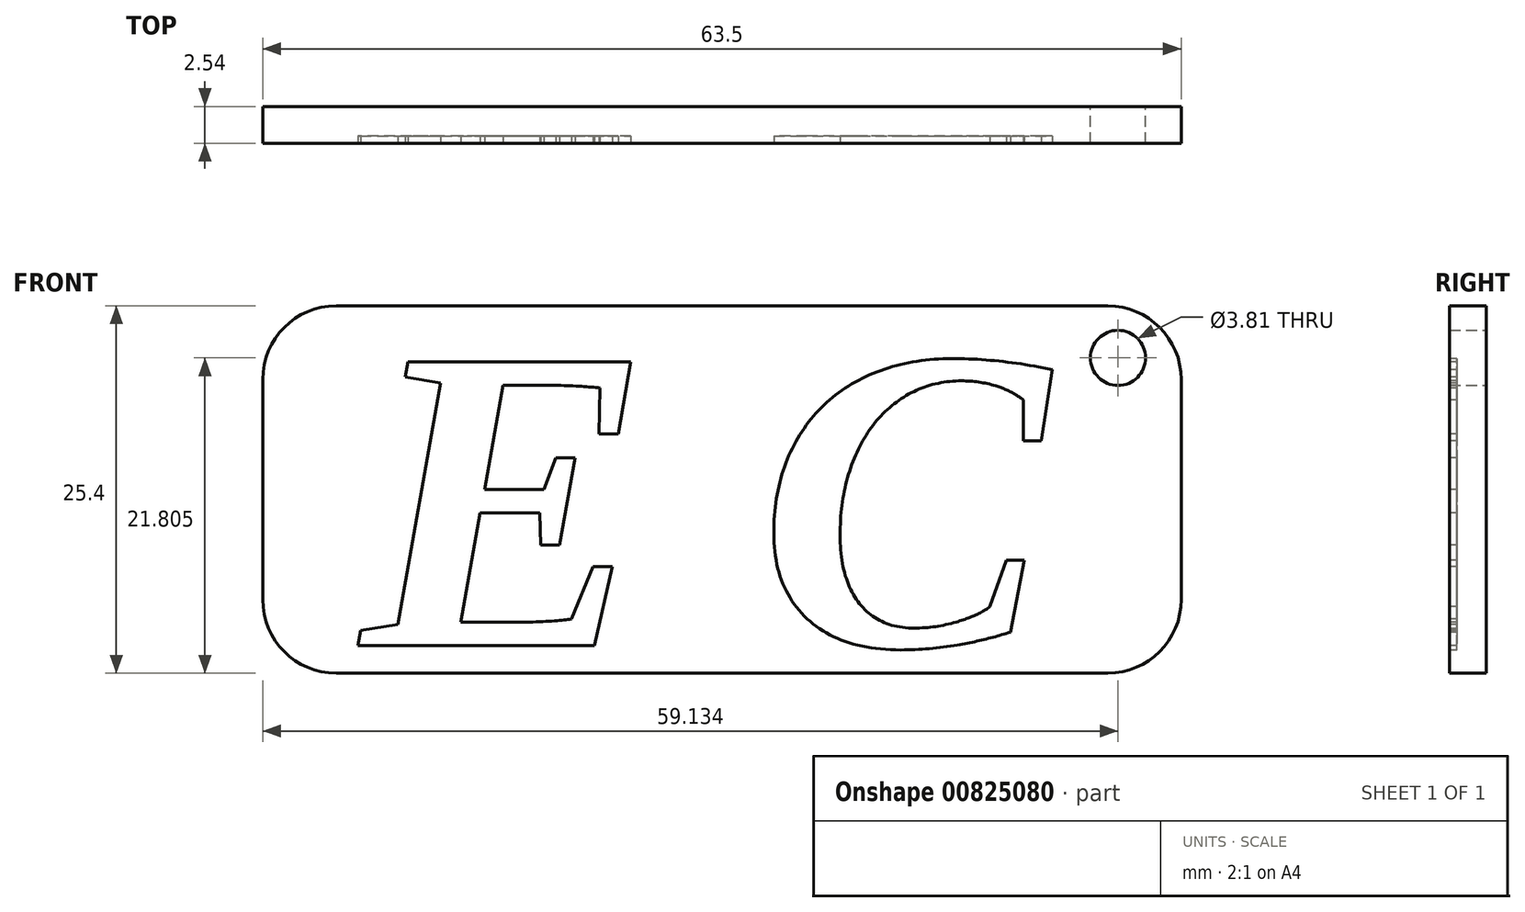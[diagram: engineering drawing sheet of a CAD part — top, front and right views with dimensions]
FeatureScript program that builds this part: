
annotation { "Feature Type Name" : "Feature", "Feature Type Description" : "" }
export const myFeature = defineFeature(function(context is Context, id is Id, definition is map)
    precondition{}
    {
        {
            var Q0;
            Q0=qCreatedBy(makeId("Front.planeOp"),FACE);
            var sketch = newSketch(context, id + "F0", { "sketchPlane" : qUnion([Q0])});
            skLineSegment(sketch, "E0.bottom", {"start": v(-31.75, 12.7) * mm, "end": v(31.75, 12.7) * mm});
            skLineSegment(sketch, "E0.top", {"start": v(-31.75, -12.7) * mm, "end": v(31.75, -12.7) * mm});
            skLineSegment(sketch, "E0.left", {"start": v(-31.75, 12.7) * mm, "end": v(-31.75, -12.7) * mm});
            skLineSegment(sketch, "E0.right", {"start": v(31.75, 12.7) * mm, "end": v(31.75, -12.7) * mm});
            skPoint(sketch, "E0.middle", {"position": v(0, 0) * mm});
            skPoint(sketch, "E1", {"position": v(27.38, 9.1) * mm});
            skSolve(sketch);
        }
        {
            var Q0;
            Q0 = qSketchRegion(id + "F0", true);
            extrude(context, id + "F1", {"entities" : qUnion([Q0]), "depth" : 2.54 * mm, "offsetDistance" : 25.4 * mm});
        }
        {
            var Q0;
            Q0=makeQuery(id+"F1.opExtrude","CAP_FACE",FACE,{"disambiguationData":[OSD([sQuery(id+"F0.wireOp",EDGE,"E0.bottom"),sQuery(id+"F0.wireOp",EDGE,"E0.top"),sQuery(id+"F0.wireOp",EDGE,"E0.left"),sQuery(id+"F0.wireOp",EDGE,"E0.right")])],"isStart":false});
            var sketch = newSketch(context, id + "F2", { "sketchPlane" : qUnion([Q0])});
            skText(sketch, "E2", { "text": "E C", "fontName": "Tinos-BoldItalic.ttf"});
            const initialGuessF2  = {"E2": [-0.02494, -0.0108, 1, 0, 0.02159]};
            skSetInitialGuess(sketch, initialGuessF2);
            skSolve(sketch);
        }
        {
            var Q0;
            Q0 = qSketchRegion(id + "F2", true);
            extrude(context, id + "F3", {"entities" : qUnion([Q0]), "operationType" : NewBodyOperationType.REMOVE, "oppositeDirection" : true, "depth" : 0.5 * mm, "offsetDistance" : 25.4 * mm});
        }
        {
            var Q0;
            Q0=makeQuery(id+"F1.opExtrude","SWEPT_EDGE",EDGE,{"disambiguationData":[OSD([sQuery(id+"F0.wireOp",EDGE,"E0.bottom"),sQuery(id+"F0.wireOp",EDGE,"E0.right")])]});
            var Q1;
            Q1=makeQuery(id+"F1.opExtrude","SWEPT_EDGE",EDGE,{"disambiguationData":[OSD([sQuery(id+"F0.wireOp",EDGE,"E0.top"),sQuery(id+"F0.wireOp",EDGE,"E0.right")])]});
            var Q2;
            Q2=makeQuery(id+"F1.opExtrude","SWEPT_EDGE",EDGE,{"disambiguationData":[OSD([sQuery(id+"F0.wireOp",EDGE,"E0.bottom"),sQuery(id+"F0.wireOp",EDGE,"E0.left")])]});
            var Q3;
            Q3=makeQuery(id+"F1.opExtrude","SWEPT_EDGE",EDGE,{"disambiguationData":[OSD([sQuery(id+"F0.wireOp",EDGE,"E0.top"),sQuery(id+"F0.wireOp",EDGE,"E0.left")])]});
            fillet(context, id + "F4", {"entities" : qUnion([Q0, Q1, Q2, Q3]), "radius" : 5.08 * mm, "tangentPropagation" : true, "allowEdgeOverflow" : false});
        }
        {
            var Q0;
            Q0=sQuery(id+"F0.wireOp",VERTEX,"E1");
            var Q1;
            Q1=makeQuery(id+"F1.opExtrude","SWEPT_BODY",BODY,{"disambiguationData":[OSD([sQuery(id+"F0.wireOp",EDGE,"E0.bottom"),sQuery(id+"F0.wireOp",EDGE,"E0.top"),sQuery(id+"F0.wireOp",EDGE,"E0.left"),sQuery(id+"F0.wireOp",EDGE,"E0.right")])]});
            hole(context, id + "F5", {"style" : HoleStyle.SIMPLE, "endStyle" : HoleEndStyle.BLIND, "oppositeDirection" : true, "holeDiameter" : 3.8 * mm, "majorDiameter" : 6.35 * mm, "holeDepth" : 12.7 * mm, "isTappedThrough" : true, "tappedDepth" : 12.7 * mm, "tapClearance" : 3, "locations" : qUnion([Q0]), "scope" : qUnion([Q1])});
        }
    });
